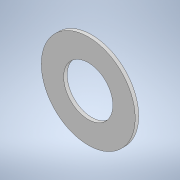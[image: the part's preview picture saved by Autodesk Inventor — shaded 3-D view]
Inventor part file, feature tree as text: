
AUTODESK INVENTOR PART (.ipt)
format: ipt  version: 2021 (Build 250183000, 183)  size: 97,792 bytes
history: native  units: mm
features: extrude x1, sketch x1
ambient origin geometry x8: Origin, YZ Plane, XZ Plane, XY Plane, X Axis, Y Axis, Z Axis, Center Point
bodies: Solid1 (feature_tree)
feature tree (2):
  extrude  "Extrusion1"  Depth=1.5mm
  sketch  "Sketch1"  dims[d0=21.0mm d1=40.0mm d2=1.5mm d3=0.0mm]
